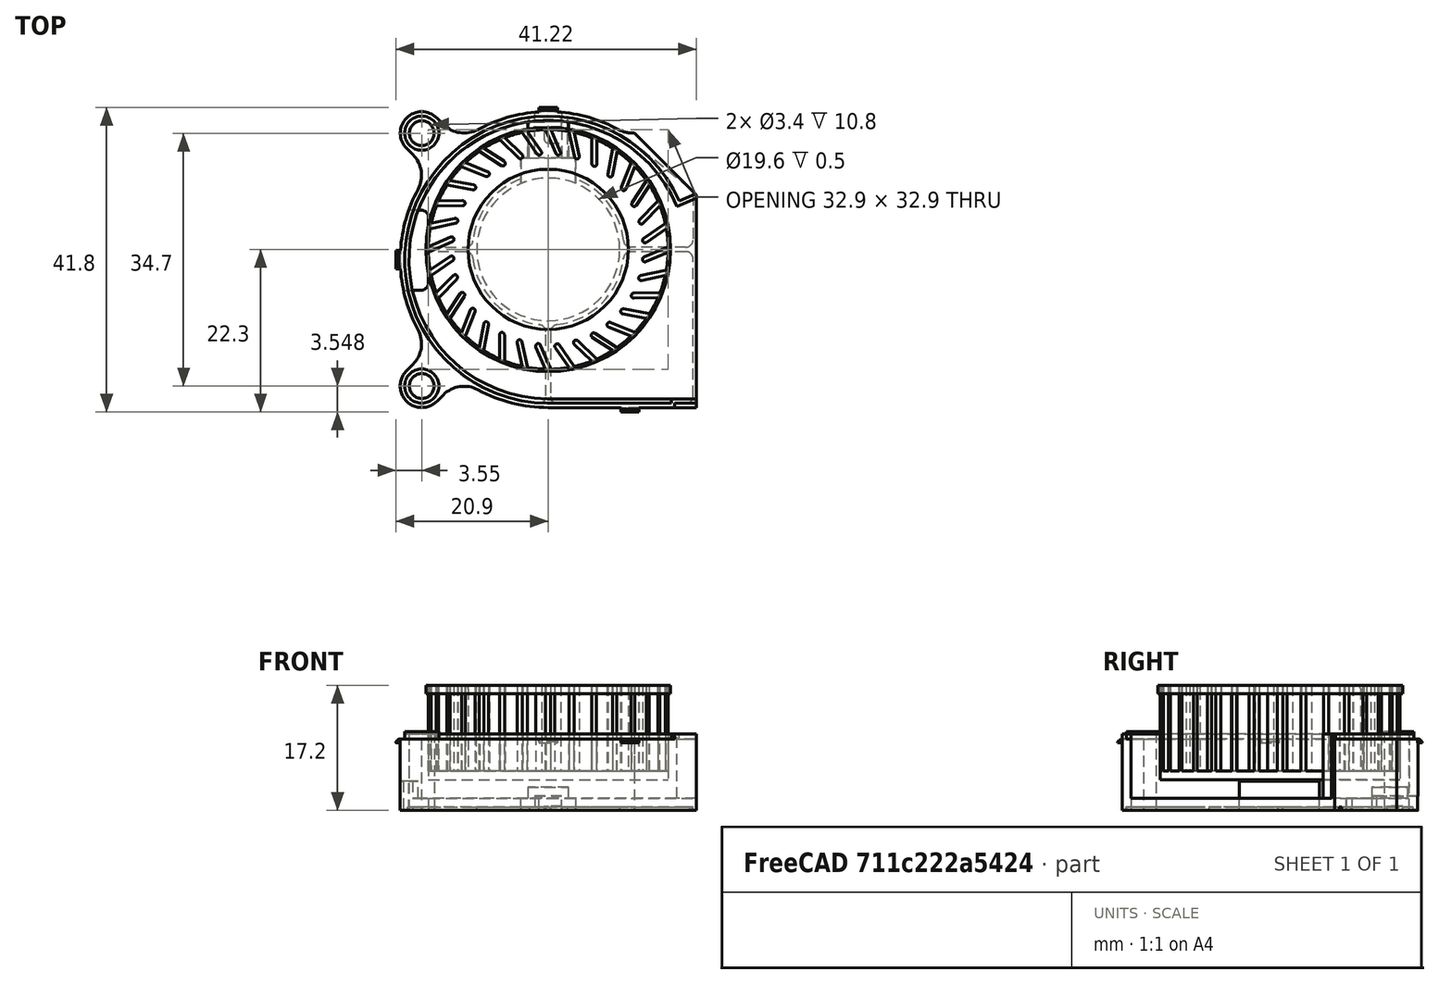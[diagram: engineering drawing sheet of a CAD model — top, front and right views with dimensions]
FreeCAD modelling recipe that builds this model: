
FCSTD DOCUMENT  (FreeCAD 2021.922R24301 +4188 (Git))
Label: 4010_fan
License: All rights reserved
LicenseURL: http://en.wikipedia.org/wiki/All_rights_reserved
objects: Part::Feature×1, Part::Box×1, Part::Cut×1, App::Part×1
note: 3 computed .brp shape members not serialized (recipe doc carries the construction recipe); baked Part::Feature solids carry a one-line shape summary decoded from their .brp

FEATURE [Part::Feature] Part__Feature420  label="4020 Blower Fan v5"
  Placement = pos=(0,0,0) rot=(0,0,-1;3.14159rad)
  shape: bbox 41.22 x 41.8 x 17.2 mm, 289 faces, 2 solids (baked)
FEATURE [Part::Box] Box  label="Würfel"
  AttacherType = Attacher::AttachEngine3D
  Height = 30
  Length = 30
  Placement = pos=(29.0122,-1.20101,-5) rot=(0,0,1;0.785398rad)
  Width = 30
FEATURE [Part::Cut] Cut  label="FAN"
  Base = -> Part__Feature420
  Refine = true
  Tool = -> Box
FEATURE [App::Part] Part  label="4010_fan"
  ExportMode = 1
  Group = -> [Cut,Box,Part__Feature420]
  Origin = -> Origin
  _ExportChildren = -> [Cut]
  _GroupVersion = 1
